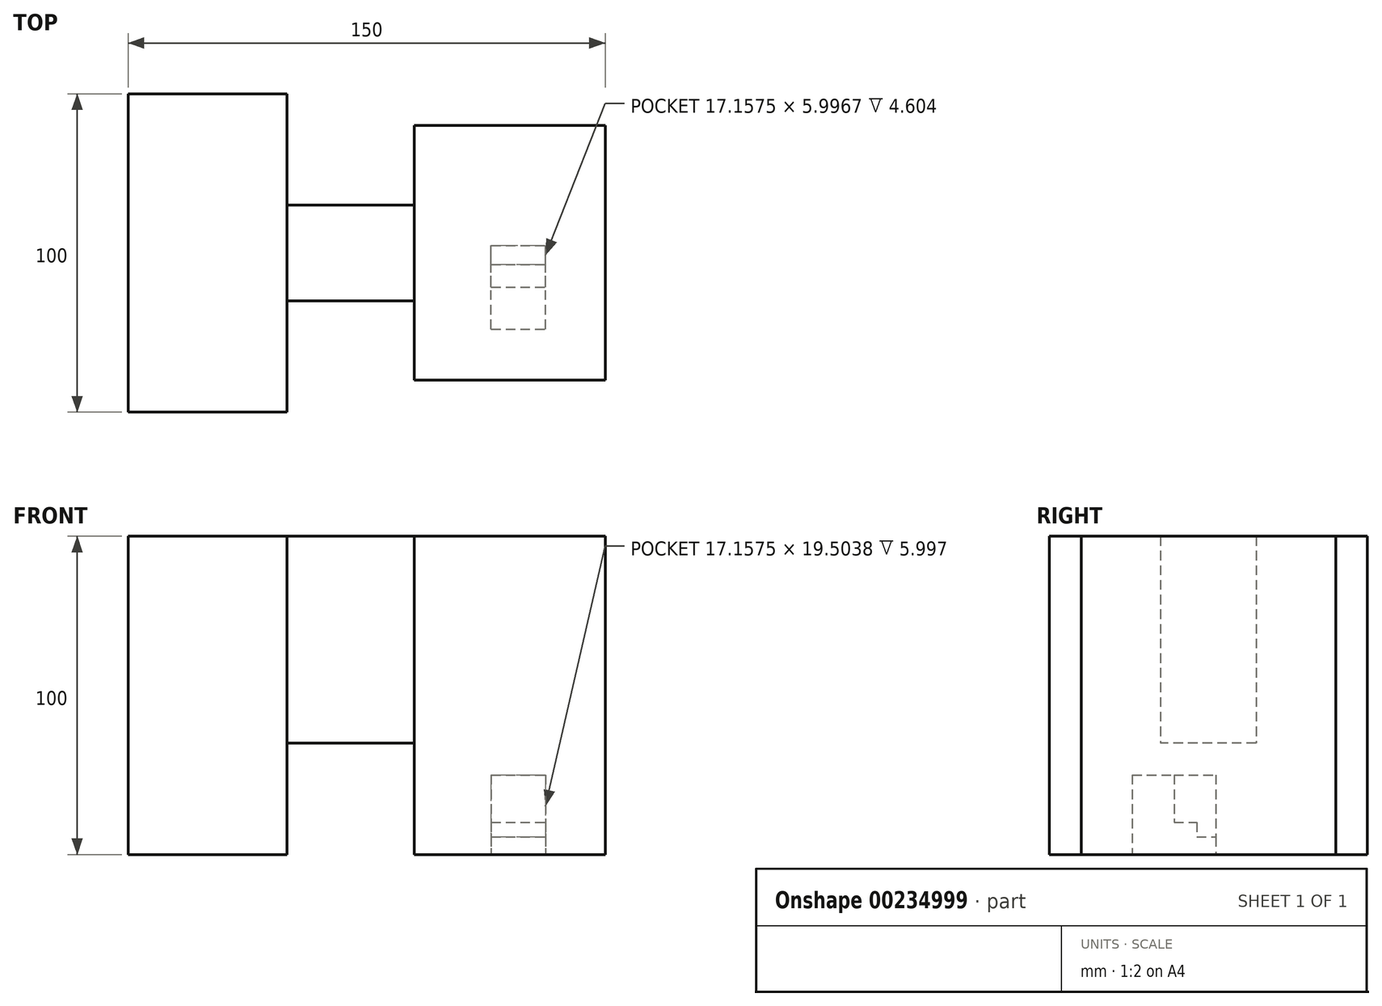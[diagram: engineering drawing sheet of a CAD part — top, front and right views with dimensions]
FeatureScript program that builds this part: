
annotation { "Feature Type Name" : "Feature", "Feature Type Description" : "" }
export const myFeature = defineFeature(function(context is Context, id is Id, definition is map)
    precondition{}
    {
        {
            var Q0;
            Q0=qCreatedBy(makeId("Top.planeOp"),FACE);
            var sketch = newSketch(context, id + "F0", { "sketchPlane" : qUnion([Q0])});
            skLineSegment(sketch, "E0.bottom", {"start": v(0, 0) * mm, "end": v(50, 0) * mm});
            skLineSegment(sketch, "E0.top", {"start": v(0, 100) * mm, "end": v(50, 100) * mm});
            skLineSegment(sketch, "E0.left", {"start": v(0, 0) * mm, "end": v(0, 100) * mm});
            skLineSegment(sketch, "E0.right", {"start": v(50, 0) * mm, "end": v(50, 100) * mm});
            skSolve(sketch);
        }
        {
            var Q0;
            Q0=makeQuery(id+"F0.imprint","IMPRINT",FACE,{"disambiguationData":[TD([[makeQuery(id+"F0.imprint","IMPRINT",EDGE,{"derivedFrom":sQuery(id+"F0.wireOp",EDGE,"E0.bottom")}),1.0]])]});
            extrude(context, id + "F1", {"entities" : qUnion([Q0]), "depth" : 100 * mm});
        }
        {
            var Q0;
            Q0=makeQuery(id+"F1.opExtrude","SWEPT_FACE",FACE,{"disambiguationData":[OSD([sQuery(id+"F0.wireOp",EDGE,"E0.right")])]});
            var sketch = newSketch(context, id + "F2", { "sketchPlane" : qUnion([Q0])});
            skLineSegment(sketch, "E1.bottom", {"start": v(65, 100) * mm, "end": v(35, 100) * mm});
            skLineSegment(sketch, "E1.top", {"start": v(65, 35) * mm, "end": v(35, 35) * mm});
            skLineSegment(sketch, "E1.left", {"start": v(65, 100) * mm, "end": v(65, 35) * mm});
            skLineSegment(sketch, "E1.right", {"start": v(35, 100) * mm, "end": v(35, 35) * mm});
            skSolve(sketch);
        }
        {
            var Q0;
            Q0=makeQuery(id+"F2.imprint","IMPRINT",FACE,{"disambiguationData":[TD([[makeQuery(id+"F2.imprint","IMPRINT",EDGE,{"derivedFrom":sQuery(id+"F2.wireOp",EDGE,"E1.bottom")}),-1.0]])]});
            extrude(context, id + "F3", {"entities" : qUnion([Q0]), "depth" : 40 * mm});
        }
        {
            var Q0;
            Q0=makeQuery(id+"F3.opExtrude","CAP_FACE",FACE,{"disambiguationData":[OSD([sQuery(id+"F2.wireOp",EDGE,"E1.bottom"),sQuery(id+"F2.wireOp",EDGE,"E1.top"),sQuery(id+"F2.wireOp",EDGE,"E1.left"),sQuery(id+"F2.wireOp",EDGE,"E1.right")])],"isStart":false});
            var sketch = newSketch(context, id + "F4", { "sketchPlane" : qUnion([Q0])});
            skLineSegment(sketch, "E2.bottom", {"start": v(90, 100) * mm, "end": v(10, 100) * mm});
            skLineSegment(sketch, "E2.top", {"start": v(90, 0) * mm, "end": v(10, 0) * mm});
            skLineSegment(sketch, "E2.left", {"start": v(90, 100) * mm, "end": v(90, 0) * mm});
            skLineSegment(sketch, "E2.right", {"start": v(10, 100) * mm, "end": v(10, 0) * mm});
            skSolve(sketch);
        }
        {
            var Q0;
            Q0 = qSketchRegion(id + "F4", true);
            extrude(context, id + "F5", {"entities" : qUnion([Q0]), "depth" : 60 * mm});
        }
        {
            var Q0;
            Q0=qCreatedBy(makeId("Top.planeOp"),FACE);
            var sketch = newSketch(context, id + "F6", { "sketchPlane" : qUnion([Q0])});
            skLineSegment(sketch, "E3.bottom", {"start": v(114.16, 26.08) * mm, "end": v(131.32, 26.08) * mm});
            skLineSegment(sketch, "E3.top", {"start": v(114.16, 52.34) * mm, "end": v(131.32, 52.34) * mm});
            skLineSegment(sketch, "E3.left", {"start": v(114.16, 26.08) * mm, "end": v(114.16, 52.34) * mm});
            skLineSegment(sketch, "E3.right", {"start": v(131.32, 26.08) * mm, "end": v(131.32, 52.34) * mm});
            skSolve(sketch);
        }
        {
            var Q0;
            Q0 = qSketchRegion(id + "F6", true);
            extrude(context, id + "F7", {"entities" : qUnion([Q0]), "depth" : 25 * mm});
        }
        {
            var Q0;
            Q0=makeQuery(id+"F7.opExtrude","SWEPT_FACE",FACE,{"disambiguationData":[OSD([sQuery(id+"F6.wireOp",EDGE,"E3.right")])]});
            var sketch = newSketch(context, id + "F8", { "sketchPlane" : qUnion([Q0])});
            skLineSegment(sketch, "E4", {"start": v(39.2, 25) * mm, "end": v(39.2, 10.1) * mm});
            skLineSegment(sketch, "E5", {"start": v(39.2, 10.1) * mm, "end": v(46.34, 10.1) * mm});
            skLineSegment(sketch, "E6", {"start": v(46.34, 10.1) * mm, "end": v(46.34, 5.5) * mm});
            skLineSegment(sketch, "E7", {"start": v(46.34, 5.5) * mm, "end": v(52.34, 5.5) * mm});
            skSolve(sketch);
        }
        {
            var Q0;
            {var subQ1=sQuery(id+"F8.wireOp",EDGE,"E4");Q0=makeQuery(id+"F8.imprint","IMPRINT",FACE,{"disambiguationData":[TD([[makeQuery(id+"F8.imprint","IMPRINT",EDGE,{"derivedFrom":subQ1}),1.0]])]});}
            extrude(context, id + "F9", {"entities" : qUnion([Q0]), "operationType" : NewBodyOperationType.REMOVE, "endBound" : BoundingType.UP_TO_NEXT, "oppositeDirection" : true, "depth" : 25 * mm});
        }
    });
